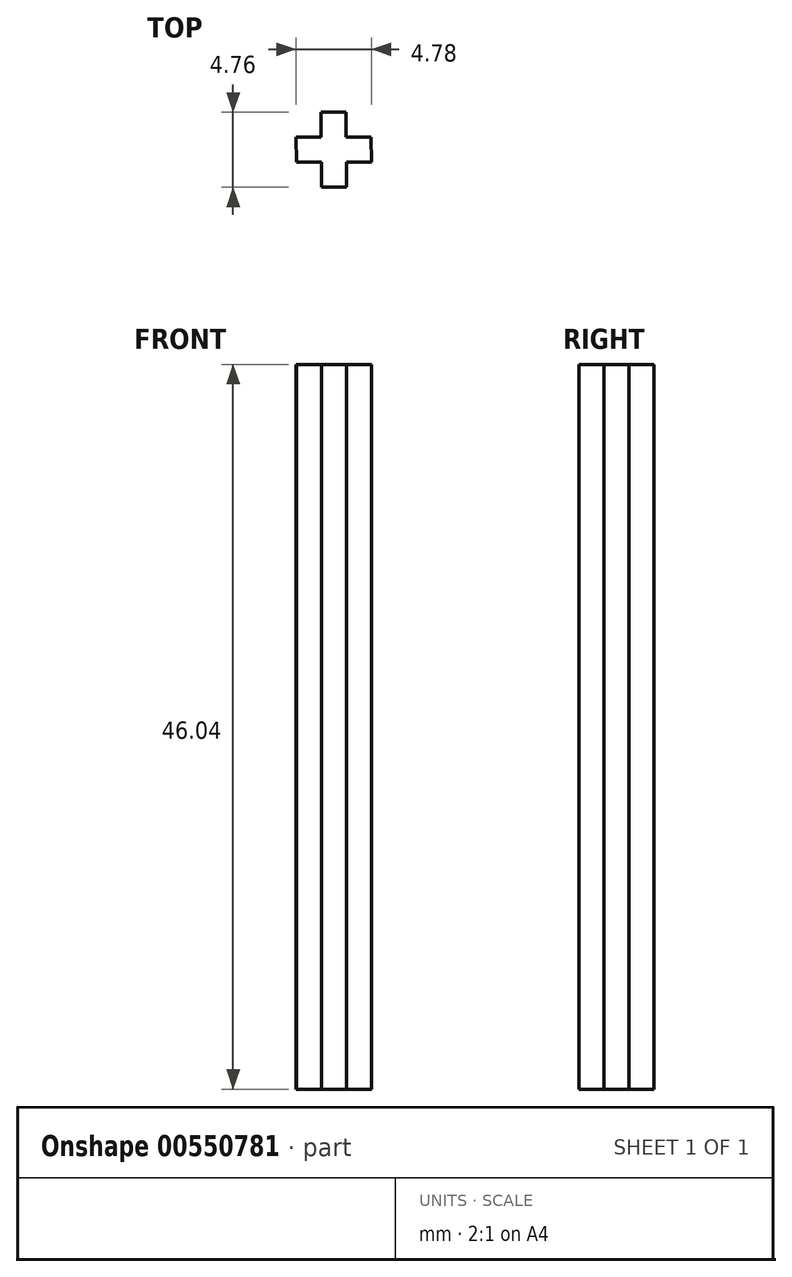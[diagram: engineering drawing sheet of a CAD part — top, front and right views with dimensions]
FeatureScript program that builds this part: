
annotation { "Feature Type Name" : "Feature", "Feature Type Description" : "" }
export const myFeature = defineFeature(function(context is Context, id is Id, definition is map)
    precondition{}
    {
        {
            var Q0;
            Q0=qCreatedBy(makeId("Top.planeOp"),FACE);
            var sketch = newSketch(context, id + "F0", { "sketchPlane" : qUnion([Q0])});
            skLineSegment(sketch, "E0.left", {"start": v(0, 0) * mm, "end": v(-0.02, 1.59) * mm});
            skLineSegment(sketch, "E0.right", {"start": v(-4.76, 0) * mm, "end": v(-4.78, 1.59) * mm});
            skLineSegment(sketch, "E1.bottom", {"start": v(-3.18, -1.59) * mm, "end": v(-1.59, -1.59) * mm});
            skLineSegment(sketch, "E1.top", {"start": v(-3.2, 3.18) * mm, "end": v(-1.6, 3.18) * mm});
            skLineSegment(sketch, "E2", {"start": v(-3.2, 3.18) * mm, "end": v(-3.2, 1.59) * mm});
            skLineSegment(sketch, "E3", {"start": v(-3.18, -1.59) * mm, "end": v(-3.18, 0) * mm});
            skLineSegment(sketch, "E4", {"start": v(-1.6, 3.18) * mm, "end": v(-1.6, 1.59) * mm});
            skLineSegment(sketch, "E5", {"start": v(-1.59, -1.59) * mm, "end": v(-1.59, 0) * mm});
            skLineSegment(sketch, "E6", {"start": v(-1.6, 1.59) * mm, "end": v(-0.02, 1.59) * mm});
            skLineSegment(sketch, "E7", {"start": v(-3.2, 1.59) * mm, "end": v(-4.78, 1.59) * mm});
            skLineSegment(sketch, "E8", {"start": v(-3.17, 0) * mm, "end": v(-4.76, 0) * mm});
            skLineSegment(sketch, "E9", {"start": v(-1.59, 0) * mm, "end": v(0, 0) * mm});
            skSolve(sketch);
        }
        {
            var Q0;
            Q0 = qSketchRegion(id + "F0", true);
            extrude(context, id + "F1", {"entities" : qUnion([Q0]), "depth" : 46.04 * mm, "offsetDistance" : 25.4 * mm});
        }
    });
